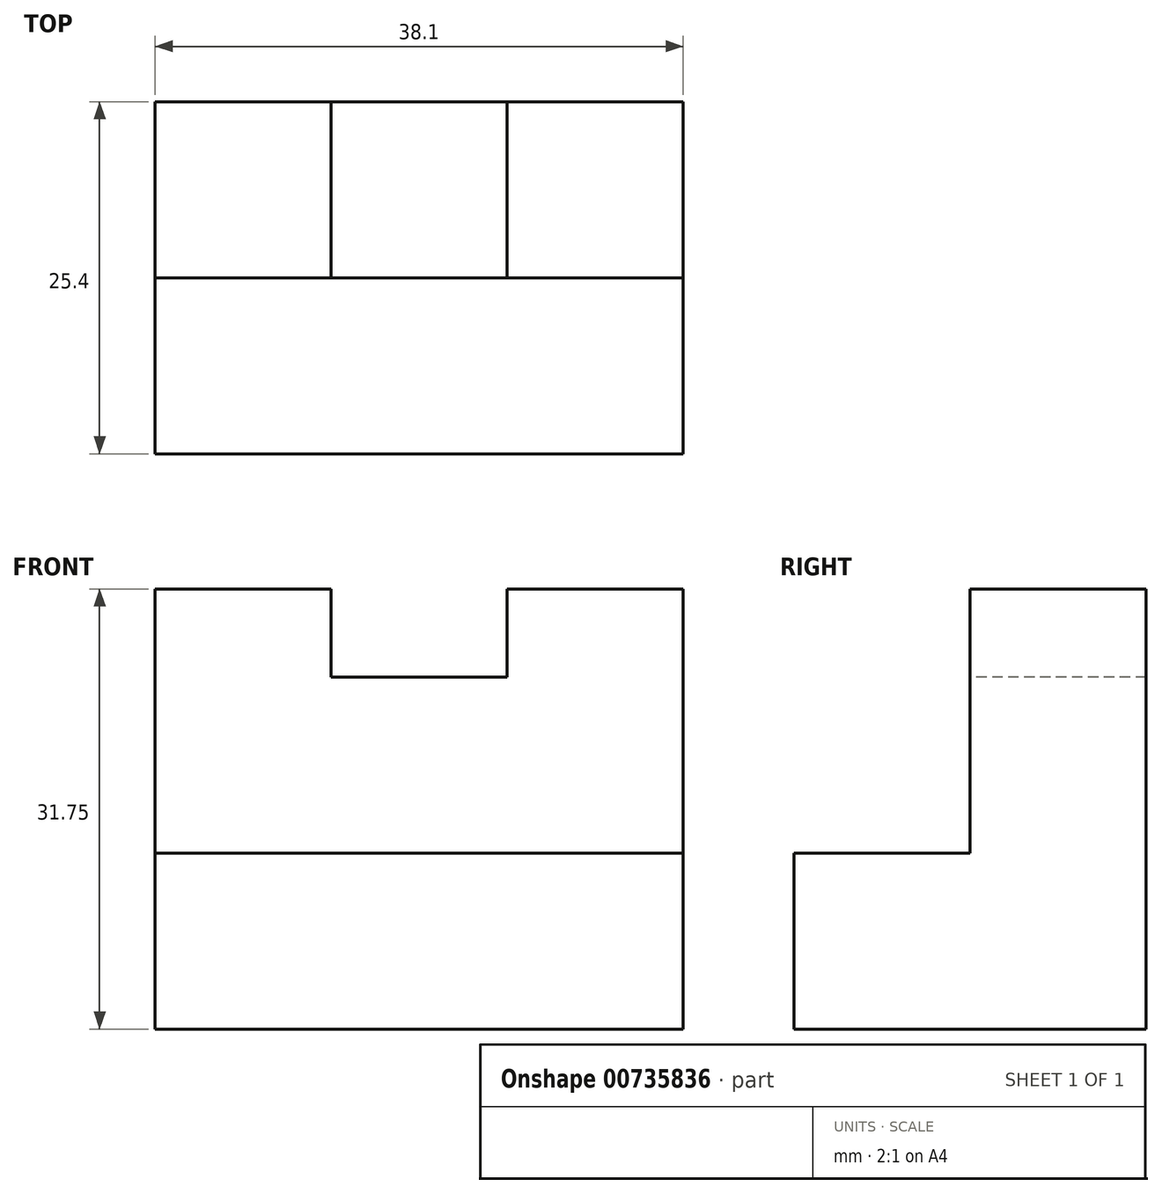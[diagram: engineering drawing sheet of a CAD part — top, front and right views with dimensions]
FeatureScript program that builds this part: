
annotation { "Feature Type Name" : "Feature", "Feature Type Description" : "" }
export const myFeature = defineFeature(function(context is Context, id is Id, definition is map)
    precondition{}
    {
        {
            var Q0;
            Q0=qCreatedBy(makeId("Right.planeOp"),FACE);
            var sketch = newSketch(context, id + "F0", { "sketchPlane" : qUnion([Q0])});
            skLineSegment(sketch, "E0", {"start": v(0, 0) * mm, "end": v(25.4, 0) * mm});
            skLineSegment(sketch, "E1", {"start": v(25.4, 0) * mm, "end": v(25.4, 31.75) * mm});
            skLineSegment(sketch, "E2", {"start": v(25.4, 31.75) * mm, "end": v(12.7, 31.75) * mm});
            skLineSegment(sketch, "E3", {"start": v(12.7, 31.75) * mm, "end": v(12.7, 12.7) * mm});
            skLineSegment(sketch, "E4", {"start": v(12.7, 12.7) * mm, "end": v(0, 12.7) * mm});
            skLineSegment(sketch, "E5", {"start": v(0, 12.7) * mm, "end": v(0, 0) * mm});
            skSolve(sketch);
        }
        {
            var Q0;
            Q0 = qSketchRegion(id + "F0", true);
            extrude(context, id + "F1", {"entities" : qUnion([Q0]), "depth" : 38.1 * mm, "offsetDistance" : 25.4 * mm});
        }
        {
            var Q0;
            Q0=qCreatedBy(makeId("Front.planeOp"),FACE);
            var sketch = newSketch(context, id + "F2", { "sketchPlane" : qUnion([Q0])});
            skLineSegment(sketch, "E6", {"start": v(12.42, 30.85) * mm, "end": v(12.42, 24.5) * mm});
            skLineSegment(sketch, "E7", {"start": v(12.42, 24.5) * mm, "end": v(25.12, 24.5) * mm});
            skLineSegment(sketch, "E8", {"start": v(25.12, 24.5) * mm, "end": v(25.12, 30.85) * mm});
            skLineSegment(sketch, "E9", {"start": v(25.12, 30.85) * mm, "end": v(12.42, 30.85) * mm});
            skSolve(sketch);
        }
        {
            var Q0;
            Q0=makeQuery(id+"F2.imprint","IMPRINT",FACE,{"disambiguationData":[TD([[makeQuery(id+"F2.imprint","IMPRINT",EDGE,{"derivedFrom":sQuery(id+"F2.wireOp",EDGE,"E6")}),1.0]])]});
            extrude(context, id + "F3", {"entities" : qUnion([Q0]), "operationType" : NewBodyOperationType.REMOVE, "oppositeDirection" : true, "depth" : 12.7 * mm, "offsetDistance" : 25.4 * mm});
        }
        {
            var Q0;
            Q0=makeQuery(id+"F1.opExtrude","SWEPT_FACE",FACE,{"disambiguationData":[OSD([sQuery(id+"F0.wireOp",EDGE,"E3")])]});
            var sketch = newSketch(context, id + "F4", { "sketchPlane" : qUnion([Q0])});
            skLineSegment(sketch, "E10", {"start": v(12.7, 31.75) * mm, "end": v(12.7, 25.4) * mm});
            skLineSegment(sketch, "E11", {"start": v(12.7, 25.4) * mm, "end": v(25.4, 25.4) * mm});
            skLineSegment(sketch, "E12", {"start": v(25.4, 25.4) * mm, "end": v(25.4, 31.75) * mm});
            skLineSegment(sketch, "E13", {"start": v(25.4, 31.75) * mm, "end": v(12.7, 31.75) * mm});
            skSolve(sketch);
        }
        {
            var Q0;
            Q0=makeQuery(id+"F4.imprint","IMPRINT",FACE,{"disambiguationData":[TD([[makeQuery(id+"F4.imprint","IMPRINT",EDGE,{"derivedFrom":sQuery(id+"F4.wireOp",EDGE,"E10")}),1.0]])]});
            extrude(context, id + "F5", {"entities" : qUnion([Q0]), "operationType" : NewBodyOperationType.REMOVE, "oppositeDirection" : true, "depth" : 25.4 * mm, "offsetDistance" : 25.4 * mm});
        }
    });
